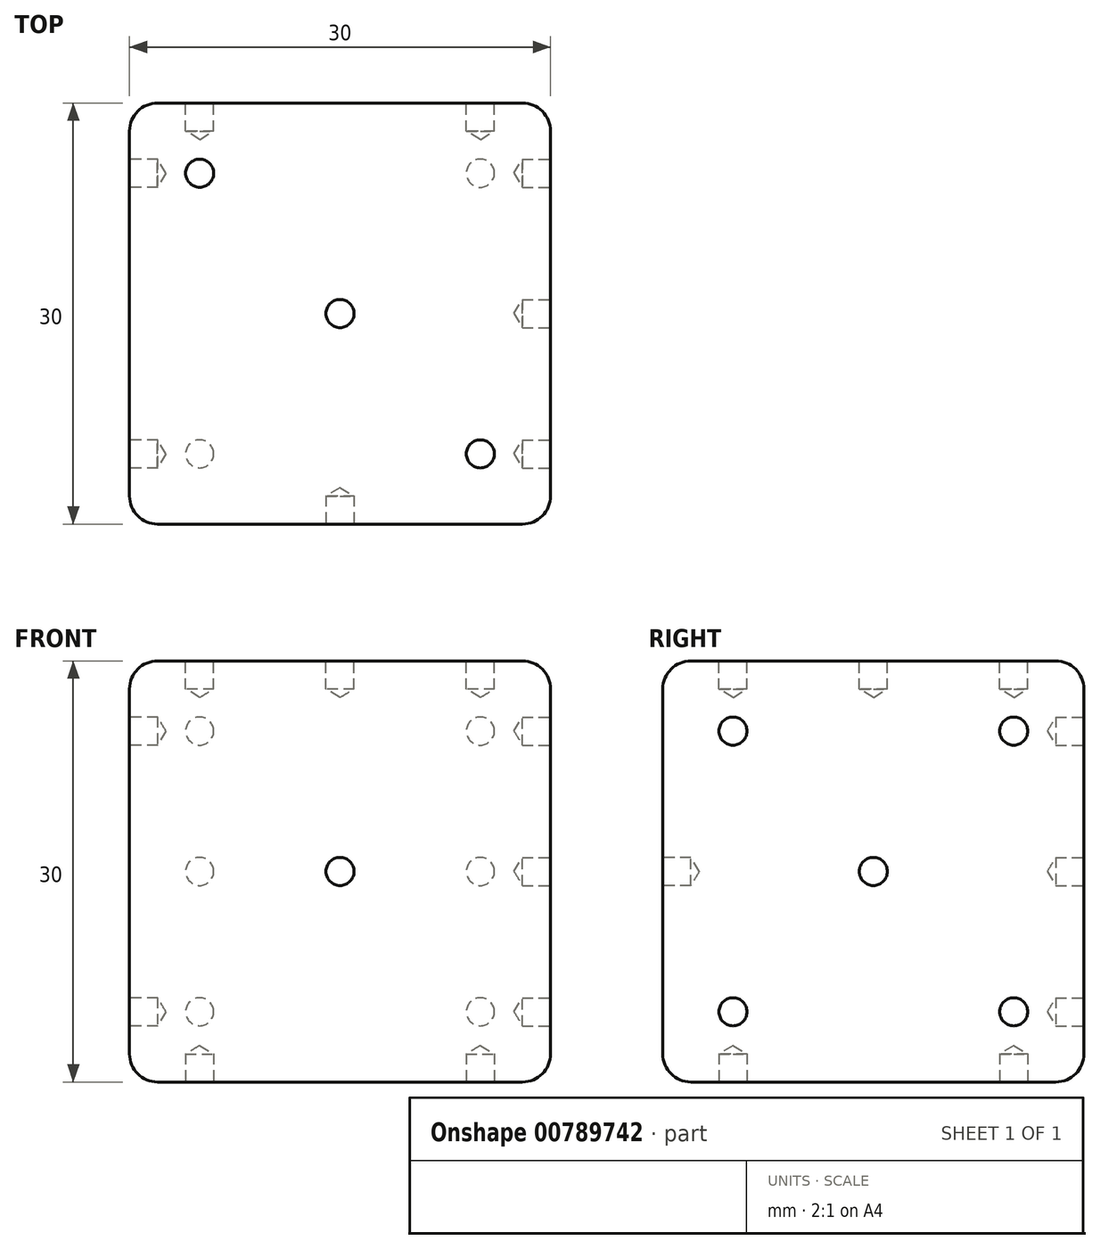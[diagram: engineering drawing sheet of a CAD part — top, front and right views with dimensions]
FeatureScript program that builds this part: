
annotation { "Feature Type Name" : "Feature", "Feature Type Description" : "" }
export const myFeature = defineFeature(function(context is Context, id is Id, definition is map)
    precondition{}
    {
        {
            var Q0;
            Q0=qCreatedBy(makeId("Front.planeOp"),FACE);
            var sketch = newSketch(context, id + "F0", { "sketchPlane" : qUnion([Q0])});
            skLineSegment(sketch, "E0.bottom", {"start": v(15, 15) * mm, "end": v(-15, 15) * mm});
            skLineSegment(sketch, "E0.top", {"start": v(15, -15) * mm, "end": v(-15, -15) * mm});
            skLineSegment(sketch, "E0.left", {"start": v(15, 15) * mm, "end": v(15, -15) * mm});
            skLineSegment(sketch, "E0.right", {"start": v(-15, 15) * mm, "end": v(-15, -15) * mm});
            skPoint(sketch, "E0.middle", {"position": v(0, 0) * mm});
            skSolve(sketch);
        }
        {
            var Q0;
            Q0 = qSketchRegion(id + "F0", true);
            extrude(context, id + "F1", {"entities" : qUnion([Q0]), "endBound" : BoundingType.SYMMETRIC, "depth" : 30 * mm, "offsetDistance" : 25 * mm});
        }
        {
            var Q0;
            Q0=makeQuery(id+"F1.opExtrude","SWEPT_EDGE",EDGE,{"disambiguationData":[OSD([sQuery(id+"F0.wireOp",EDGE,"E0.bottom"),sQuery(id+"F0.wireOp",EDGE,"E0.left")])]});
            var Q1;
            Q1=makeQuery(id+"F1.opExtrude","CAP_EDGE",EDGE,{"disambiguationData":[OSD([sQuery(id+"F0.wireOp",EDGE,"E0.bottom")])],"isStart":false});
            var Q2;
            Q2=makeQuery(id+"F1.opExtrude","CAP_EDGE",EDGE,{"disambiguationData":[OSD([sQuery(id+"F0.wireOp",EDGE,"E0.bottom")])],"isStart":true});
            var Q3;
            Q3=makeQuery(id+"F1.opExtrude","SWEPT_EDGE",EDGE,{"disambiguationData":[OSD([sQuery(id+"F0.wireOp",EDGE,"E0.bottom"),sQuery(id+"F0.wireOp",EDGE,"E0.right")])]});
            var Q4;
            Q4=makeQuery(id+"F1.opExtrude","CAP_EDGE",EDGE,{"disambiguationData":[OSD([sQuery(id+"F0.wireOp",EDGE,"E0.right")])],"isStart":true});
            var Q5;
            Q5=makeQuery(id+"F1.opExtrude","CAP_EDGE",EDGE,{"disambiguationData":[OSD([sQuery(id+"F0.wireOp",EDGE,"E0.left")])],"isStart":true});
            var Q6;
            Q6=makeQuery(id+"F1.opExtrude","CAP_EDGE",EDGE,{"disambiguationData":[OSD([sQuery(id+"F0.wireOp",EDGE,"E0.left")])],"isStart":false});
            var Q7;
            Q7=makeQuery(id+"F1.opExtrude","SWEPT_EDGE",EDGE,{"disambiguationData":[OSD([sQuery(id+"F0.wireOp",EDGE,"E0.top"),sQuery(id+"F0.wireOp",EDGE,"E0.left")])]});
            var Q8;
            Q8=makeQuery(id+"F1.opExtrude","CAP_EDGE",EDGE,{"disambiguationData":[OSD([sQuery(id+"F0.wireOp",EDGE,"E0.top")])],"isStart":false});
            var Q9;
            Q9=makeQuery(id+"F1.opExtrude","CAP_EDGE",EDGE,{"disambiguationData":[OSD([sQuery(id+"F0.wireOp",EDGE,"E0.top")])],"isStart":true});
            var Q10;
            Q10=makeQuery(id+"F1.opExtrude","CAP_EDGE",EDGE,{"disambiguationData":[OSD([sQuery(id+"F0.wireOp",EDGE,"E0.right")])],"isStart":false});
            var Q11;
            Q11=makeQuery(id+"F1.opExtrude","SWEPT_EDGE",EDGE,{"disambiguationData":[OSD([sQuery(id+"F0.wireOp",EDGE,"E0.top"),sQuery(id+"F0.wireOp",EDGE,"E0.right")])]});
            fillet(context, id + "F2", {"entities" : qUnion([Q0, Q1, Q2, Q3, Q4, Q5, Q6, Q7, Q8, Q9, Q10, Q11]), "radius" : 2 * mm, "tangentPropagation" : true, "allowEdgeOverflow" : false});
        }
        {
            var Q0;
            Q0=makeQuery(id+"F1.opExtrude","SWEPT_FACE",FACE,{"disambiguationData":[OSD([sQuery(id+"F0.wireOp",EDGE,"E0.top")])]});
            var sketch = newSketch(context, id + "F3", { "sketchPlane" : qUnion([Q0])});
            skCircle(sketch, "E1", {"center": v(-10, -10) * mm, "radius": 1 * mm});
            skCircle(sketch, "E2", {"center": v(-10, 10) * mm, "radius": 1 * mm});
            skCircle(sketch, "E3", {"center": v(10, -10) * mm, "radius": 1 * mm});
            skCircle(sketch, "E4", {"center": v(10, 10) * mm, "radius": 1 * mm});
            skSolve(sketch);
        }
        {
            var Q0;
            Q0=sQuery(id+"F3.wireOp",VERTEX,"E1.center");
            var Q1;
            Q1=sQuery(id+"F3.wireOp",VERTEX,"E2.center");
            var Q2;
            Q2=sQuery(id+"F3.wireOp",VERTEX,"E4.center");
            var Q3;
            Q3=sQuery(id+"F3.wireOp",VERTEX,"E3.center");
            var Q4;
            Q4=makeQuery(id+"F1.opExtrude","SWEPT_BODY",BODY,{"disambiguationData":[OSD([sQuery(id+"F0.wireOp",EDGE,"E0.bottom"),sQuery(id+"F0.wireOp",EDGE,"E0.top"),sQuery(id+"F0.wireOp",EDGE,"E0.left"),sQuery(id+"F0.wireOp",EDGE,"E0.right")])]});
            hole(context, id + "F4", {"style" : HoleStyle.SIMPLE, "endStyle" : HoleEndStyle.BLIND, "holeDiameter" : 2 * mm, "majorDiameter" : 5 * mm, "holeDepth" : 2 * mm, "isTappedThrough" : true, "tappedDepth" : 12 * mm, "tapClearance" : 3, "locations" : qUnion([Q0, Q1, Q2, Q3]), "scope" : qUnion([Q4])});
        }
        {
            var Q0;
            Q0=makeQuery(id+"F1.opExtrude","CAP_FACE",FACE,{"disambiguationData":[OSD([sQuery(id+"F0.wireOp",EDGE,"E0.bottom"),sQuery(id+"F0.wireOp",EDGE,"E0.top"),sQuery(id+"F0.wireOp",EDGE,"E0.left"),sQuery(id+"F0.wireOp",EDGE,"E0.right")])],"isStart":true});
            var sketch = newSketch(context, id + "F5", { "sketchPlane" : qUnion([Q0])});
            skCircle(sketch, "E5", {"center": v(-10, -10) * mm, "radius": 1 * mm});
            skCircle(sketch, "E6", {"center": v(-10, 10) * mm, "radius": 1 * mm});
            skCircle(sketch, "E7", {"center": v(10, -10) * mm, "radius": 1 * mm});
            skCircle(sketch, "E8", {"center": v(10, 10) * mm, "radius": 1 * mm});
            skCircle(sketch, "E9", {"center": v(10, 0) * mm, "radius": 1 * mm});
            skCircle(sketch, "E10", {"center": v(-10, 0) * mm, "radius": 1 * mm});
            skSolve(sketch);
        }
        {
            var Q0;
            Q0=sQuery(id+"F5.wireOp",VERTEX,"E7.center");
            var Q1;
            Q1=sQuery(id+"F5.wireOp",VERTEX,"E5.center");
            var Q2;
            Q2=sQuery(id+"F5.wireOp",VERTEX,"E9.center");
            var Q3;
            Q3=sQuery(id+"F5.wireOp",VERTEX,"E8.center");
            var Q4;
            Q4=sQuery(id+"F5.wireOp",VERTEX,"E10.center");
            var Q5;
            Q5=sQuery(id+"F5.wireOp",VERTEX,"E6.center");
            var Q6;
            Q6=makeQuery(id+"F1.opExtrude","SWEPT_BODY",BODY,{"disambiguationData":[OSD([sQuery(id+"F0.wireOp",EDGE,"E0.bottom"),sQuery(id+"F0.wireOp",EDGE,"E0.top"),sQuery(id+"F0.wireOp",EDGE,"E0.left"),sQuery(id+"F0.wireOp",EDGE,"E0.right")])]});
            hole(context, id + "F6", {"style" : HoleStyle.SIMPLE, "endStyle" : HoleEndStyle.BLIND, "holeDiameter" : 2 * mm, "majorDiameter" : 5 * mm, "holeDepth" : 2 * mm, "isTappedThrough" : true, "tappedDepth" : 12 * mm, "tapClearance" : 3, "locations" : qUnion([Q0, Q1, Q2, Q3, Q4, Q5]), "scope" : qUnion([Q6])});
        }
        {
            var Q0;
            Q0=makeQuery(id+"F1.opExtrude","SWEPT_FACE",FACE,{"disambiguationData":[OSD([sQuery(id+"F0.wireOp",EDGE,"E0.bottom")])]});
            var sketch = newSketch(context, id + "F7", { "sketchPlane" : qUnion([Q0])});
            skCircle(sketch, "E11", {"center": v(0, 0) * mm, "radius": 1 * mm});
            skCircle(sketch, "E12", {"center": v(-10, 10) * mm, "radius": 1 * mm});
            skCircle(sketch, "E13", {"center": v(10, -10) * mm, "radius": 1 * mm});
            skSolve(sketch);
        }
        {
            var Q0;
            Q0=sQuery(id+"F7.wireOp",VERTEX,"E11.center");
            var Q1;
            Q1=sQuery(id+"F7.wireOp",VERTEX,"E13.center");
            var Q2;
            Q2=sQuery(id+"F7.wireOp",VERTEX,"E12.center");
            var Q3;
            Q3=makeQuery(id+"F1.opExtrude","SWEPT_BODY",BODY,{"disambiguationData":[OSD([sQuery(id+"F0.wireOp",EDGE,"E0.bottom"),sQuery(id+"F0.wireOp",EDGE,"E0.top"),sQuery(id+"F0.wireOp",EDGE,"E0.left"),sQuery(id+"F0.wireOp",EDGE,"E0.right")])]});
            hole(context, id + "F8", {"style" : HoleStyle.SIMPLE, "endStyle" : HoleEndStyle.BLIND, "holeDiameter" : 2 * mm, "majorDiameter" : 5 * mm, "holeDepth" : 2 * mm, "isTappedThrough" : true, "tappedDepth" : 12 * mm, "tapClearance" : 3, "locations" : qUnion([Q0, Q1, Q2]), "scope" : qUnion([Q3])});
        }
        {
            var Q0;
            Q0=makeQuery(id+"F1.opExtrude","SWEPT_FACE",FACE,{"disambiguationData":[OSD([sQuery(id+"F0.wireOp",EDGE,"E0.left")])]});
            var sketch = newSketch(context, id + "F9", { "sketchPlane" : qUnion([Q0])});
            skCircle(sketch, "E14", {"center": v(-10, -10) * mm, "radius": 1 * mm});
            skCircle(sketch, "E15", {"center": v(-10, 10) * mm, "radius": 1 * mm});
            skCircle(sketch, "E16", {"center": v(10, -10) * mm, "radius": 1 * mm});
            skCircle(sketch, "E17", {"center": v(10, 10) * mm, "radius": 1 * mm});
            skCircle(sketch, "E18", {"center": v(0, 0) * mm, "radius": 1 * mm});
            skSolve(sketch);
        }
        {
            var Q0;
            Q0=sQuery(id+"F9.wireOp",VERTEX,"E14.center");
            var Q1;
            Q1=sQuery(id+"F9.wireOp",VERTEX,"E16.center");
            var Q2;
            Q2=sQuery(id+"F9.wireOp",VERTEX,"E18.center");
            var Q3;
            Q3=sQuery(id+"F9.wireOp",VERTEX,"E15.center");
            var Q4;
            Q4=sQuery(id+"F9.wireOp",VERTEX,"E17.center");
            var Q5;
            Q5=makeQuery(id+"F1.opExtrude","SWEPT_BODY",BODY,{"disambiguationData":[OSD([sQuery(id+"F0.wireOp",EDGE,"E0.bottom"),sQuery(id+"F0.wireOp",EDGE,"E0.top"),sQuery(id+"F0.wireOp",EDGE,"E0.left"),sQuery(id+"F0.wireOp",EDGE,"E0.right")])]});
            hole(context, id + "F10", {"style" : HoleStyle.SIMPLE, "endStyle" : HoleEndStyle.BLIND, "holeDiameter" : 2 * mm, "majorDiameter" : 5 * mm, "holeDepth" : 2 * mm, "isTappedThrough" : true, "tappedDepth" : 12 * mm, "tapClearance" : 3, "locations" : qUnion([Q0, Q1, Q2, Q3, Q4]), "scope" : qUnion([Q5])});
        }
        {
            var Q0;
            Q0=makeQuery(id+"F1.opExtrude","SWEPT_FACE",FACE,{"disambiguationData":[OSD([sQuery(id+"F0.wireOp",EDGE,"E0.right")])]});
            var sketch = newSketch(context, id + "F11", { "sketchPlane" : qUnion([Q0])});
            skCircle(sketch, "E19", {"center": v(-10, -10) * mm, "radius": 1 * mm});
            skCircle(sketch, "E20", {"center": v(10, 10) * mm, "radius": 1 * mm});
            skSolve(sketch);
        }
        {
            var Q0;
            Q0=sQuery(id+"F11.wireOp",VERTEX,"E19.center");
            var Q1;
            Q1=sQuery(id+"F11.wireOp",VERTEX,"E20.center");
            var Q2;
            Q2=makeQuery(id+"F1.opExtrude","SWEPT_BODY",BODY,{"disambiguationData":[OSD([sQuery(id+"F0.wireOp",EDGE,"E0.bottom"),sQuery(id+"F0.wireOp",EDGE,"E0.top"),sQuery(id+"F0.wireOp",EDGE,"E0.left"),sQuery(id+"F0.wireOp",EDGE,"E0.right")])]});
            hole(context, id + "F12", {"style" : HoleStyle.SIMPLE, "endStyle" : HoleEndStyle.BLIND, "holeDiameter" : 2 * mm, "majorDiameter" : 5 * mm, "holeDepth" : 2 * mm, "isTappedThrough" : true, "tappedDepth" : 12 * mm, "tapClearance" : 3, "locations" : qUnion([Q0, Q1]), "scope" : qUnion([Q2])});
        }
        {
            var Q0;
            Q0=makeQuery(id+"F1.opExtrude","CAP_FACE",FACE,{"disambiguationData":[OSD([sQuery(id+"F0.wireOp",EDGE,"E0.bottom"),sQuery(id+"F0.wireOp",EDGE,"E0.top"),sQuery(id+"F0.wireOp",EDGE,"E0.left"),sQuery(id+"F0.wireOp",EDGE,"E0.right")])],"isStart":false});
            var sketch = newSketch(context, id + "F13", { "sketchPlane" : qUnion([Q0])});
            skCircle(sketch, "E21", {"center": v(0, 0) * mm, "radius": 1 * mm});
            skSolve(sketch);
        }
        {
            var Q0;
            Q0=sQuery(id+"F13.wireOp",VERTEX,"E21.center");
            var Q1;
            Q1=makeQuery(id+"F1.opExtrude","SWEPT_BODY",BODY,{"disambiguationData":[OSD([sQuery(id+"F0.wireOp",EDGE,"E0.bottom"),sQuery(id+"F0.wireOp",EDGE,"E0.top"),sQuery(id+"F0.wireOp",EDGE,"E0.left"),sQuery(id+"F0.wireOp",EDGE,"E0.right")])]});
            hole(context, id + "F14", {"style" : HoleStyle.SIMPLE, "endStyle" : HoleEndStyle.BLIND, "holeDiameter" : 2 * mm, "majorDiameter" : 5 * mm, "holeDepth" : 2 * mm, "isTappedThrough" : true, "tappedDepth" : 12 * mm, "tapClearance" : 3, "locations" : qUnion([Q0]), "scope" : qUnion([Q1])});
        }
    });
